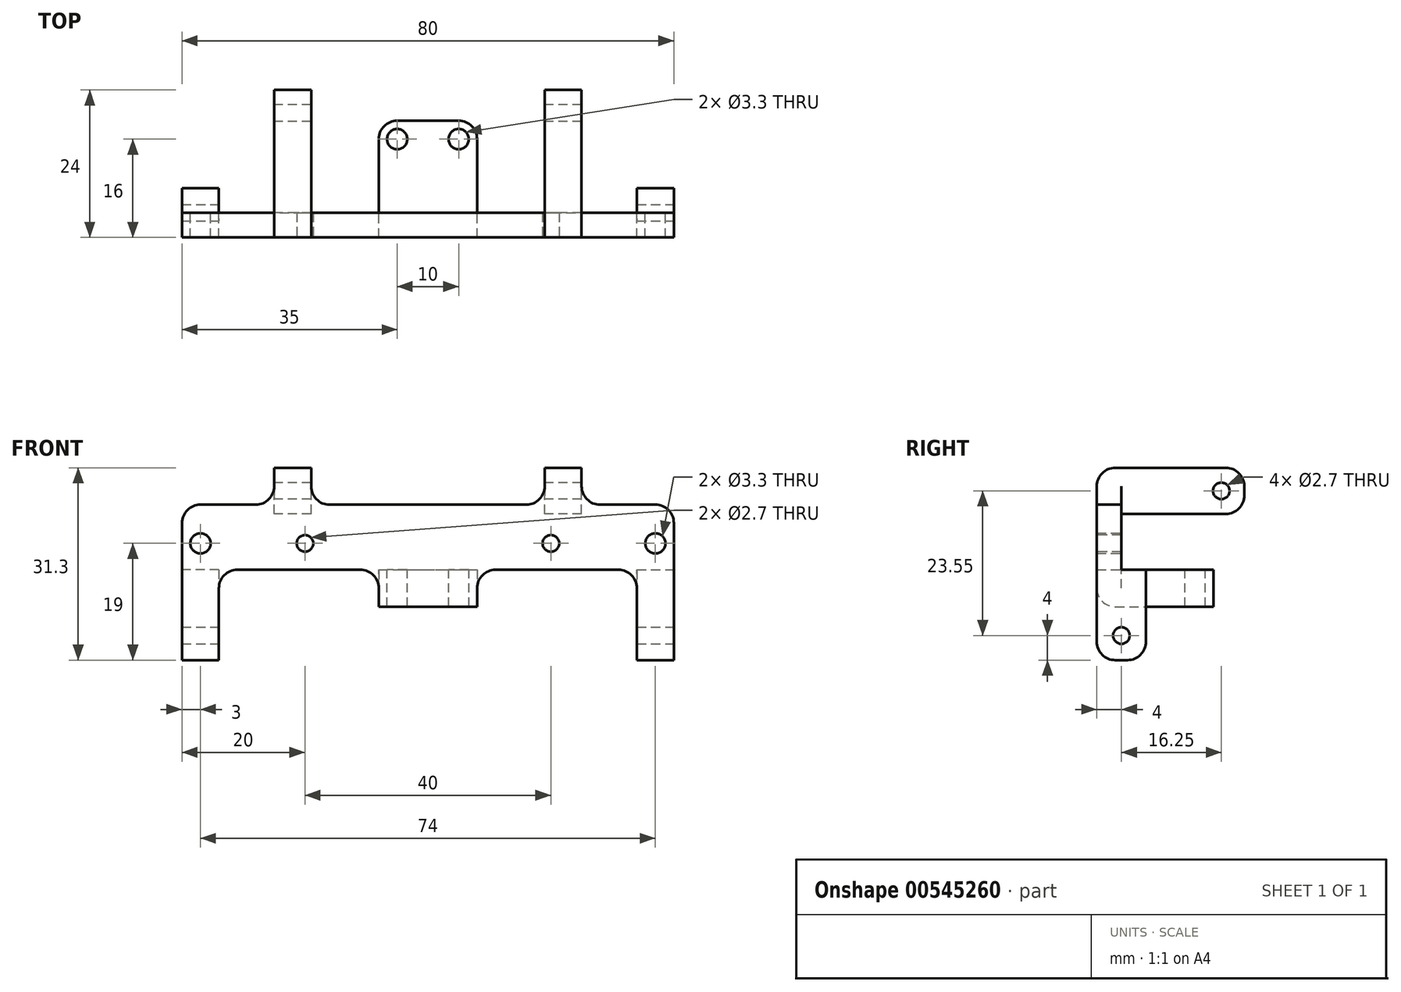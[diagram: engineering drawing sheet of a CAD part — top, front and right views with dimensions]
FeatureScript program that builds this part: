
annotation { "Feature Type Name" : "Feature", "Feature Type Description" : "" }
export const myFeature = defineFeature(function(context is Context, id is Id, definition is map)
    precondition{}
    {
        {
            var Q0;
            Q0=qCreatedBy(makeId("Front.planeOp"),FACE);
            var sketch = newSketch(context, id + "F0", { "sketchPlane" : qUnion([Q0])});
            skLineSegment(sketch, "E0.bottom", {"start": v(-40, 6.3) * mm, "end": v(-25, 6.3) * mm});
            skLineSegment(sketch, "E0.top", {"start": v(-34, -4.3) * mm, "end": v(-8, -4.3) * mm});
            skLineSegment(sketch, "E0.left", {"start": v(-40, 6.3) * mm, "end": v(-40, -4.3) * mm});
            skLineSegment(sketch, "E0.right", {"start": v(40, 6.3) * mm, "end": v(40, -4.3) * mm});
            skLineSegment(sketch, "E1.top", {"start": v(-40, -19) * mm, "end": v(-34, -19) * mm});
            skLineSegment(sketch, "E1.left", {"start": v(-40, -4.3) * mm, "end": v(-40, -19) * mm});
            skLineSegment(sketch, "E1.right", {"start": v(-34, -4.3) * mm, "end": v(-34, -19) * mm});
            skLineSegment(sketch, "E2.MirrorCS", {"start": v(34, -4.3) * mm, "end": v(34, -19) * mm});
            skLineSegment(sketch, "E3.MirrorCS", {"start": v(40, -19) * mm, "end": v(34, -19) * mm});
            skLineSegment(sketch, "E4.MirrorCS", {"start": v(40, -4.3) * mm, "end": v(40, -19) * mm});
            skCircle(sketch, "E5", {"center": v(-37, 0) * mm, "radius": 1.65 * mm});
            skCircle(sketch, "E6", {"center": v(37, 0) * mm, "radius": 1.65 * mm});
            skLineSegment(sketch, "E7.bottom", {"start": v(-25, 12.3) * mm, "end": v(-19, 12.3) * mm});
            skLineSegment(sketch, "E7.left", {"start": v(-25, 12.3) * mm, "end": v(-25, 6.3) * mm});
            skLineSegment(sketch, "E7.right", {"start": v(-19, 12.3) * mm, "end": v(-19, 6.3) * mm});
            skLineSegment(sketch, "E8.MirrorCS", {"start": v(19, 12.3) * mm, "end": v(19, 6.3) * mm});
            skLineSegment(sketch, "E9.MirrorCS", {"start": v(25, 12.3) * mm, "end": v(19, 12.3) * mm});
            skLineSegment(sketch, "E10.MirrorCS", {"start": v(25, 12.3) * mm, "end": v(25, 6.3) * mm});
            skLineSegment(sketch, "E11.trimOffspring", {"start": v(-19, 6.3) * mm, "end": v(19, 6.3) * mm});
            skLineSegment(sketch, "E12.trimOffspring", {"start": v(25, 6.3) * mm, "end": v(40, 6.3) * mm});
            skLineSegment(sketch, "E13.top", {"start": v(8, -10.3) * mm, "end": v(-8, -10.3) * mm});
            skLineSegment(sketch, "E13.left", {"start": v(8, -4.3) * mm, "end": v(8, -10.3) * mm});
            skLineSegment(sketch, "E13.right", {"start": v(-8, -4.3) * mm, "end": v(-8, -10.3) * mm});
            skLineSegment(sketch, "E14.trimOffspring", {"start": v(8, -4.3) * mm, "end": v(34, -4.3) * mm});
            skSolve(sketch);
        }
        {
            var Q0;
            Q0=makeQuery(id+"F0.imprint","IMPRINT",FACE,{"disambiguationData":[TD([[makeQuery(id+"F0.imprint","IMPRINT",EDGE,{"derivedFrom":sQuery(id+"F0.wireOp",EDGE,"E0.bottom")}),-1.0]])]});
            extrude(context, id + "F1", {"entities" : qUnion([Q0]), "depth" : 4 * mm, "offsetDistance" : 25 * mm});
        }
        {
            var Q0;
            Q0=makeQuery(id+"F1.opExtrude","CAP_FACE",FACE,{"disambiguationData":[OSD([sQuery(id+"F0.wireOp",EDGE,"E0.bottom"),sQuery(id+"F0.wireOp",EDGE,"E0.top"),sQuery(id+"F0.wireOp",EDGE,"E0.left"),sQuery(id+"F0.wireOp",EDGE,"E0.right"),sQuery(id+"F0.wireOp",EDGE,"E1.top"),sQuery(id+"F0.wireOp",EDGE,"E1.left"),sQuery(id+"F0.wireOp",EDGE,"E1.right"),sQuery(id+"F0.wireOp",EDGE,"E2.MirrorCS"),sQuery(id+"F0.wireOp",EDGE,"E3.MirrorCS"),sQuery(id+"F0.wireOp",EDGE,"E4.MirrorCS"),sQuery(id+"F0.wireOp",EDGE,"E5"),sQuery(id+"F0.wireOp",EDGE,"E6")])],"isStart":true});
            var sketch = newSketch(context, id + "F2", { "sketchPlane" : qUnion([Q0])});
            skLineSegment(sketch, "E15", {"start": v(34, -4.3) * mm, "end": v(-40, -4.3) * mm});
            skLineSegment(sketch, "E16", {"start": v(34, -4.3) * mm, "end": v(40, -4.3) * mm});
            skSolve(sketch);
        }
        {
            var Q0;
            {var subQ0=sQuery(id+"F2.wireOp",EDGE,"E16");Q0=makeQuery(id+"F2.imprint","IMPRINT",FACE,{"disambiguationData":[TD([[makeQuery(id+"F2.imprint","IMPRINT",EDGE,{"derivedFrom":subQ0}),-1.0]])]});}
            var Q1;
            {var subQ0=sQuery(id+"F2.wireOp",EDGE,"E15");Q1=makeQuery(id+"F2.imprint","IMPRINT",FACE,{"disambiguationData":[TD([[makeQuery(id+"F2.imprint","IMPRINT",EDGE,{"derivedFrom":subQ0}),1.0]])]});}
            extrude(context, id + "F3", {"entities" : qUnion([Q0, Q1]), "operationType" : NewBodyOperationType.ADD, "depth" : 4 * mm, "offsetDistance" : 25 * mm});
        }
        {
            var Q0;
            Q0=makeQuery(id+"F1.opExtrude","CAP_FACE",FACE,{"disambiguationData":[OSD([sQuery(id+"F0.wireOp",EDGE,"E0.bottom"),sQuery(id+"F0.wireOp",EDGE,"E0.top"),sQuery(id+"F0.wireOp",EDGE,"E0.left"),sQuery(id+"F0.wireOp",EDGE,"E0.right"),sQuery(id+"F0.wireOp",EDGE,"E1.top"),sQuery(id+"F0.wireOp",EDGE,"E1.left"),sQuery(id+"F0.wireOp",EDGE,"E1.right"),sQuery(id+"F0.wireOp",EDGE,"E2.MirrorCS"),sQuery(id+"F0.wireOp",EDGE,"E3.MirrorCS"),sQuery(id+"F0.wireOp",EDGE,"E4.MirrorCS"),sQuery(id+"F0.wireOp",EDGE,"E5"),sQuery(id+"F0.wireOp",EDGE,"E6"),sQuery(id+"F0.wireOp",EDGE,"E7.bottom"),sQuery(id+"F0.wireOp",EDGE,"E7.left"),sQuery(id+"F0.wireOp",EDGE,"E7.right"),sQuery(id+"F0.wireOp",EDGE,"E8.MirrorCS"),sQuery(id+"F0.wireOp",EDGE,"E9.MirrorCS"),sQuery(id+"F0.wireOp",EDGE,"E10.MirrorCS"),sQuery(id+"F0.wireOp",EDGE,"E11.trimOffspring"),sQuery(id+"F0.wireOp",EDGE,"E12.trimOffspring")])],"isStart":true});
            var sketch = newSketch(context, id + "F4", { "sketchPlane" : qUnion([Q0])});
            skLineSegment(sketch, "E17", {"start": v(-25, 6.3) * mm, "end": v(-19, 6.3) * mm});
            skLineSegment(sketch, "E18", {"start": v(19, 6.3) * mm, "end": v(25, 6.3) * mm});
            skSolve(sketch);
        }
        {
            var Q0;
            Q0=makeQuery(id+"F4.imprint","IMPRINT",FACE,{"disambiguationData":[TD([[makeQuery(id+"F4.imprint","IMPRINT",EDGE,{"derivedFrom":sQuery(id+"F4.wireOp",EDGE,"E17")}),1.0]])]});
            var Q1;
            Q1=makeQuery(id+"F4.imprint","IMPRINT",FACE,{"disambiguationData":[TD([[makeQuery(id+"F4.imprint","IMPRINT",EDGE,{"derivedFrom":sQuery(id+"F4.wireOp",EDGE,"E18")}),1.0]])]});
            extrude(context, id + "F5", {"entities" : qUnion([Q0, Q1]), "operationType" : NewBodyOperationType.ADD, "depth" : 20 * mm, "offsetDistance" : 25 * mm});
        }
        {
            var Q0;
            Q0=makeQuery(id+"F5.opExtrude","SWEPT_FACE",FACE,{"disambiguationData":[OSD([sQuery(id+"F4.wireOp",EDGE,"E17")])]});
            var Q1;
            Q1=makeQuery(id+"F5.opExtrude","SWEPT_FACE",FACE,{"disambiguationData":[OSD([sQuery(id+"F4.wireOp",EDGE,"E18")])]});
            extrude(context, id + "F6", {"entities" : qUnion([Q0, Q1]), "operationType" : NewBodyOperationType.ADD, "depth" : 1.5 * mm, "offsetDistance" : 25 * mm});
        }
        {
            var Q0;
            Q0=makeQuery(id+"F3.opExtrude","CAP_FACE",FACE,{"disambiguationData":[OSD([sQuery(id+"F0.wireOp",EDGE,"E13.top"),sQuery(id+"F0.wireOp",EDGE,"E13.left"),sQuery(id+"F0.wireOp",EDGE,"E13.right"),sQuery(id+"F2.wireOp",EDGE,"E15")])],"isStart":false});
            extrude(context, id + "F7", {"entities" : qUnion([Q0]), "operationType" : NewBodyOperationType.ADD, "depth" : 11 * mm, "offsetDistance" : 25 * mm});
        }
        {
            var Q0;
            {var subQ0=sQuery(id+"F2.wireOp",EDGE,"E15");Q0=makeQuery(id+"F7.boolean.opBoolean","MERGE",FACE,{"derivedFrom":[makeQuery(id+"F3.opExtrude","SWEPT_FACE",FACE,{"disambiguationData":[OSD([subQ0]),TDD([makeQuery(id+"F2.imprint","IMPRINT",EDGE,{"disambiguationData":[TD([[makeQuery(id+"F2.imprint","INTERSECT",VERTEX,{"derivedFrom":[makeQuery(id+"F1.opExtrude","CAP_EDGE",EDGE,{"disambiguationData":[OSD([sQuery(id+"F0.wireOp",EDGE,"E13.right")])],"isStart":true}),subQ0]}),-1.0]])],"derivedFrom":subQ0})])]}),makeQuery(id+"F7.opExtrude","SWEPT_FACE",FACE,{"disambiguationData":[OSD([subQ0])]})]});}
            var sketch = newSketch(context, id + "F8", { "sketchPlane" : qUnion([Q0])});
            skCircle(sketch, "E19", {"center": v(5, 12) * mm, "radius": 1.65 * mm});
            skCircle(sketch, "E20", {"center": v(-5, 12) * mm, "radius": 1.65 * mm});
            skSolve(sketch);
        }
        {
            var Q0;
            Q0=makeQuery(id+"F8.imprint","IMPRINT",FACE,{"disambiguationData":[TD([[makeQuery(id+"F8.imprint","IMPRINT",EDGE,{"derivedFrom":sQuery(id+"F8.wireOp",EDGE,"E19")}),1.0]])]});
            var Q1;
            Q1=makeQuery(id+"F8.imprint","IMPRINT",FACE,{"disambiguationData":[TD([[makeQuery(id+"F8.imprint","IMPRINT",EDGE,{"derivedFrom":sQuery(id+"F8.wireOp",EDGE,"E20")}),1.0]])]});
            extrude(context, id + "F9", {"entities" : qUnion([Q0, Q1]), "operationType" : NewBodyOperationType.REMOVE, "endBound" : BoundingType.THROUGH_ALL, "oppositeDirection" : true, "depth" : 25 * mm, "offsetDistance" : 25 * mm});
        }
        {
            var Q0;
            {var subQ0=sQuery(id+"F0.wireOp",EDGE,"E4.MirrorCS");var subQ1=sQuery(id+"F0.wireOp",EDGE,"E0.right");Q0=makeQuery(id+"F3.boolean.opBoolean","MERGE",FACE,{"derivedFrom":[makeQuery(id+"F1.opExtrude","SWEPT_FACE",FACE,{"disambiguationData":[OSD([subQ1,subQ0])]}),makeQuery(id+"F3.opExtrude","SWEPT_FACE",FACE,{"disambiguationData":[OSD([subQ1,subQ0])]})]});}
            var sketch = newSketch(context, id + "F10", { "sketchPlane" : qUnion([Q0])});
            skCircle(sketch, "E21", {"center": v(0, -15) * mm, "radius": 1.35 * mm});
            skSolve(sketch);
        }
        {
            var Q0;
            Q0=makeQuery(id+"F10.imprint","IMPRINT",FACE,{"disambiguationData":[TD([[makeQuery(id+"F10.imprint","IMPRINT",EDGE,{"derivedFrom":sQuery(id+"F10.wireOp",EDGE,"E21")}),1.0]])]});
            extrude(context, id + "F11", {"entities" : qUnion([Q0]), "operationType" : NewBodyOperationType.REMOVE, "endBound" : BoundingType.THROUGH_ALL, "oppositeDirection" : true, "depth" : 25 * mm, "offsetDistance" : 25 * mm});
        }
        {
            var Q0;
            {var subQ0=sQuery(id+"F0.wireOp",EDGE,"E7.left");Q0=makeQuery(id+"F6.boolean.opBoolean","MERGE",FACE,{"derivedFrom":[makeQuery(id+"F5.boolean.opBoolean","MERGE",FACE,{"derivedFrom":[makeQuery(id+"F1.opExtrude","SWEPT_FACE",FACE,{"disambiguationData":[OSD([subQ0])]}),makeQuery(id+"F5.opExtrude","SWEPT_FACE",FACE,{"disambiguationData":[OSD([subQ0])]})]}),makeQuery(id+"F6.opExtrude","SWEPT_FACE",FACE,{"disambiguationData":[OSD([sQuery(id+"F0.wireOp",EDGE,"E0.bottom"),subQ0,sQuery(id+"F4.wireOp",EDGE,"E18")])]})]});}
            var sketch = newSketch(context, id + "F12", { "sketchPlane" : qUnion([Q0])});
            skCircle(sketch, "E22", {"center": v(-16.25, 8.55) * mm, "radius": 1.35 * mm});
            skSolve(sketch);
        }
        {
            var Q0;
            Q0=makeQuery(id+"F12.imprint","IMPRINT",FACE,{"disambiguationData":[TD([[makeQuery(id+"F12.imprint","IMPRINT",EDGE,{"derivedFrom":sQuery(id+"F12.wireOp",EDGE,"E22")}),1.0]])]});
            extrude(context, id + "F13", {"entities" : qUnion([Q0]), "operationType" : NewBodyOperationType.REMOVE, "endBound" : BoundingType.THROUGH_ALL, "oppositeDirection" : true, "depth" : 25 * mm, "offsetDistance" : 25 * mm});
        }
        {
            var Q0;
            Q0=makeQuery(id+"F1.opExtrude","CAP_EDGE",EDGE,{"disambiguationData":[OSD([sQuery(id+"F0.wireOp",EDGE,"E1.top")])],"isStart":false});
            var Q1;
            Q1=makeQuery(id+"F1.opExtrude","CAP_EDGE",EDGE,{"disambiguationData":[OSD([sQuery(id+"F0.wireOp",EDGE,"E3.MirrorCS")])],"isStart":false});
            var Q2;
            Q2=makeQuery(id+"F3.opExtrude","CAP_EDGE",EDGE,{"disambiguationData":[OSD([sQuery(id+"F0.wireOp",EDGE,"E3.MirrorCS")])],"isStart":false});
            var Q3;
            Q3=makeQuery(id+"F3.opExtrude","CAP_EDGE",EDGE,{"disambiguationData":[OSD([sQuery(id+"F0.wireOp",EDGE,"E1.top")])],"isStart":false});
            var Q4;
            Q4=makeQuery(id+"F7.opExtrude","CAP_EDGE",EDGE,{"disambiguationData":[OSD([sQuery(id+"F0.wireOp",EDGE,"E13.left")])],"isStart":false});
            var Q5;
            Q5=makeQuery(id+"F7.opExtrude","CAP_EDGE",EDGE,{"disambiguationData":[OSD([sQuery(id+"F0.wireOp",EDGE,"E13.right")])],"isStart":false});
            var Q6;
            Q6=makeQuery(id+"F5.opExtrude","CAP_EDGE",EDGE,{"disambiguationData":[OSD([sQuery(id+"F0.wireOp",EDGE,"E7.bottom")])],"isStart":false});
            var Q7;
            Q7=makeQuery(id+"F5.opExtrude","CAP_EDGE",EDGE,{"disambiguationData":[OSD([sQuery(id+"F0.wireOp",EDGE,"E9.MirrorCS")])],"isStart":false});
            var Q8;
            {var subQ0=sQuery(id+"F4.wireOp",EDGE,"E18");Q8=makeQuery(id+"F6.opExtrude","CAP_EDGE",EDGE,{"disambiguationData":[OSD([subQ0]),TDD([makeQuery(id+"F5.opExtrude","CAP_EDGE",EDGE,{"disambiguationData":[OSD([subQ0])],"isStart":false})])],"isStart":false});}
            var Q9;
            {var subQ0=sQuery(id+"F4.wireOp",EDGE,"E17");Q9=makeQuery(id+"F6.opExtrude","CAP_EDGE",EDGE,{"disambiguationData":[OSD([subQ0]),TDD([makeQuery(id+"F5.opExtrude","CAP_EDGE",EDGE,{"disambiguationData":[OSD([subQ0])],"isStart":false})])],"isStart":false});}
            var Q10;
            Q10=makeQuery(id+"F1.opExtrude","CAP_EDGE",EDGE,{"disambiguationData":[OSD([sQuery(id+"F0.wireOp",EDGE,"E7.bottom")])],"isStart":false});
            var Q11;
            Q11=makeQuery(id+"F1.opExtrude","CAP_EDGE",EDGE,{"disambiguationData":[OSD([sQuery(id+"F0.wireOp",EDGE,"E9.MirrorCS")])],"isStart":false});
            var Q12;
            Q12=makeQuery(id+"F1.opExtrude","SWEPT_EDGE",EDGE,{"disambiguationData":[OSD([sQuery(id+"F0.wireOp",EDGE,"E0.top"),sQuery(id+"F0.wireOp",EDGE,"E1.right")])]});
            var Q13;
            Q13=makeQuery(id+"F1.opExtrude","SWEPT_EDGE",EDGE,{"disambiguationData":[OSD([sQuery(id+"F0.wireOp",EDGE,"E2.MirrorCS"),sQuery(id+"F0.wireOp",EDGE,"E14.trimOffspring")])]});
            var Q14;
            Q14=makeQuery(id+"F1.opExtrude","SWEPT_EDGE",EDGE,{"disambiguationData":[OSD([sQuery(id+"F0.wireOp",EDGE,"E0.top"),sQuery(id+"F0.wireOp",EDGE,"E13.right")])]});
            var Q15;
            Q15=makeQuery(id+"F1.opExtrude","SWEPT_EDGE",EDGE,{"disambiguationData":[OSD([sQuery(id+"F0.wireOp",EDGE,"E13.left"),sQuery(id+"F0.wireOp",EDGE,"E14.trimOffspring")])]});
            var Q16;
            Q16=makeQuery(id+"F1.opExtrude","SWEPT_EDGE",EDGE,{"disambiguationData":[OSD([sQuery(id+"F0.wireOp",EDGE,"E0.bottom"),sQuery(id+"F0.wireOp",EDGE,"E7.left")])]});
            var Q17;
            Q17=makeQuery(id+"F1.opExtrude","SWEPT_EDGE",EDGE,{"disambiguationData":[OSD([sQuery(id+"F0.wireOp",EDGE,"E8.MirrorCS"),sQuery(id+"F0.wireOp",EDGE,"E11.trimOffspring")])]});
            var Q18;
            Q18=makeQuery(id+"F1.opExtrude","SWEPT_EDGE",EDGE,{"disambiguationData":[OSD([sQuery(id+"F0.wireOp",EDGE,"E7.right"),sQuery(id+"F0.wireOp",EDGE,"E11.trimOffspring")])]});
            var Q19;
            Q19=makeQuery(id+"F1.opExtrude","SWEPT_EDGE",EDGE,{"disambiguationData":[OSD([sQuery(id+"F0.wireOp",EDGE,"E10.MirrorCS"),sQuery(id+"F0.wireOp",EDGE,"E12.trimOffspring")])]});
            var Q20;
            Q20=makeQuery(id+"F1.opExtrude","SWEPT_EDGE",EDGE,{"disambiguationData":[OSD([sQuery(id+"F0.wireOp",EDGE,"E0.bottom"),sQuery(id+"F0.wireOp",EDGE,"E0.left")])]});
            var Q21;
            Q21=makeQuery(id+"F1.opExtrude","SWEPT_EDGE",EDGE,{"disambiguationData":[OSD([sQuery(id+"F0.wireOp",EDGE,"E0.right"),sQuery(id+"F0.wireOp",EDGE,"E12.trimOffspring")])]});
            var Q22;
            Q22=makeQuery(id+"F1.opExtrude","CAP_EDGE",EDGE,{"disambiguationData":[OSD([sQuery(id+"F0.wireOp",EDGE,"E13.top")])],"isStart":false});
            fillet(context, id + "F14", {"entities" : qUnion([Q0, Q1, Q2, Q3, Q4, Q5, Q6, Q7, Q8, Q9, Q10, Q11, Q12, Q13, Q14, Q15, Q16, Q17, Q18, Q19, Q20, Q21, Q22]), "radius" : 3 * mm, "tangentPropagation" : true, "allowEdgeOverflow" : false});
        }
        {
            var Q0;
            Q0=makeQuery(id+"F1.opExtrude","CAP_FACE",FACE,{"disambiguationData":[OSD([sQuery(id+"F0.wireOp",EDGE,"E0.bottom"),sQuery(id+"F0.wireOp",EDGE,"E0.top"),sQuery(id+"F0.wireOp",EDGE,"E0.left"),sQuery(id+"F0.wireOp",EDGE,"E0.right"),sQuery(id+"F0.wireOp",EDGE,"E1.top"),sQuery(id+"F0.wireOp",EDGE,"E1.left"),sQuery(id+"F0.wireOp",EDGE,"E1.right"),sQuery(id+"F0.wireOp",EDGE,"E2.MirrorCS"),sQuery(id+"F0.wireOp",EDGE,"E3.MirrorCS"),sQuery(id+"F0.wireOp",EDGE,"E4.MirrorCS"),sQuery(id+"F0.wireOp",EDGE,"E5"),sQuery(id+"F0.wireOp",EDGE,"E6"),sQuery(id+"F0.wireOp",EDGE,"E7.bottom"),sQuery(id+"F0.wireOp",EDGE,"E7.left"),sQuery(id+"F0.wireOp",EDGE,"E7.right"),sQuery(id+"F0.wireOp",EDGE,"E8.MirrorCS"),sQuery(id+"F0.wireOp",EDGE,"E9.MirrorCS"),sQuery(id+"F0.wireOp",EDGE,"E10.MirrorCS"),sQuery(id+"F0.wireOp",EDGE,"E11.trimOffspring"),sQuery(id+"F0.wireOp",EDGE,"E12.trimOffspring"),sQuery(id+"F0.wireOp",EDGE,"E13.top"),sQuery(id+"F0.wireOp",EDGE,"E13.left"),sQuery(id+"F0.wireOp",EDGE,"E13.right"),sQuery(id+"F0.wireOp",EDGE,"E14.trimOffspring")])],"isStart":false});
            var sketch = newSketch(context, id + "F15", { "sketchPlane" : qUnion([Q0])});
            skCircle(sketch, "E23", {"center": v(-20, 0) * mm, "radius": 1.35 * mm});
            skCircle(sketch, "E24", {"center": v(20, 0) * mm, "radius": 1.35 * mm});
            skSolve(sketch);
        }
        {
            var Q0;
            Q0=makeQuery(id+"F15.imprint","IMPRINT",FACE,{"disambiguationData":[TD([[makeQuery(id+"F15.imprint","IMPRINT",EDGE,{"derivedFrom":sQuery(id+"F15.wireOp",EDGE,"E23")}),1.0]])]});
            var Q1;
            Q1=makeQuery(id+"F15.imprint","IMPRINT",FACE,{"disambiguationData":[TD([[makeQuery(id+"F15.imprint","IMPRINT",EDGE,{"derivedFrom":sQuery(id+"F15.wireOp",EDGE,"E24")}),1.0]])]});
            extrude(context, id + "F16", {"entities" : qUnion([Q0, Q1]), "operationType" : NewBodyOperationType.REMOVE, "endBound" : BoundingType.THROUGH_ALL, "oppositeDirection" : true, "depth" : 25 * mm, "offsetDistance" : 25 * mm});
        }
    });
